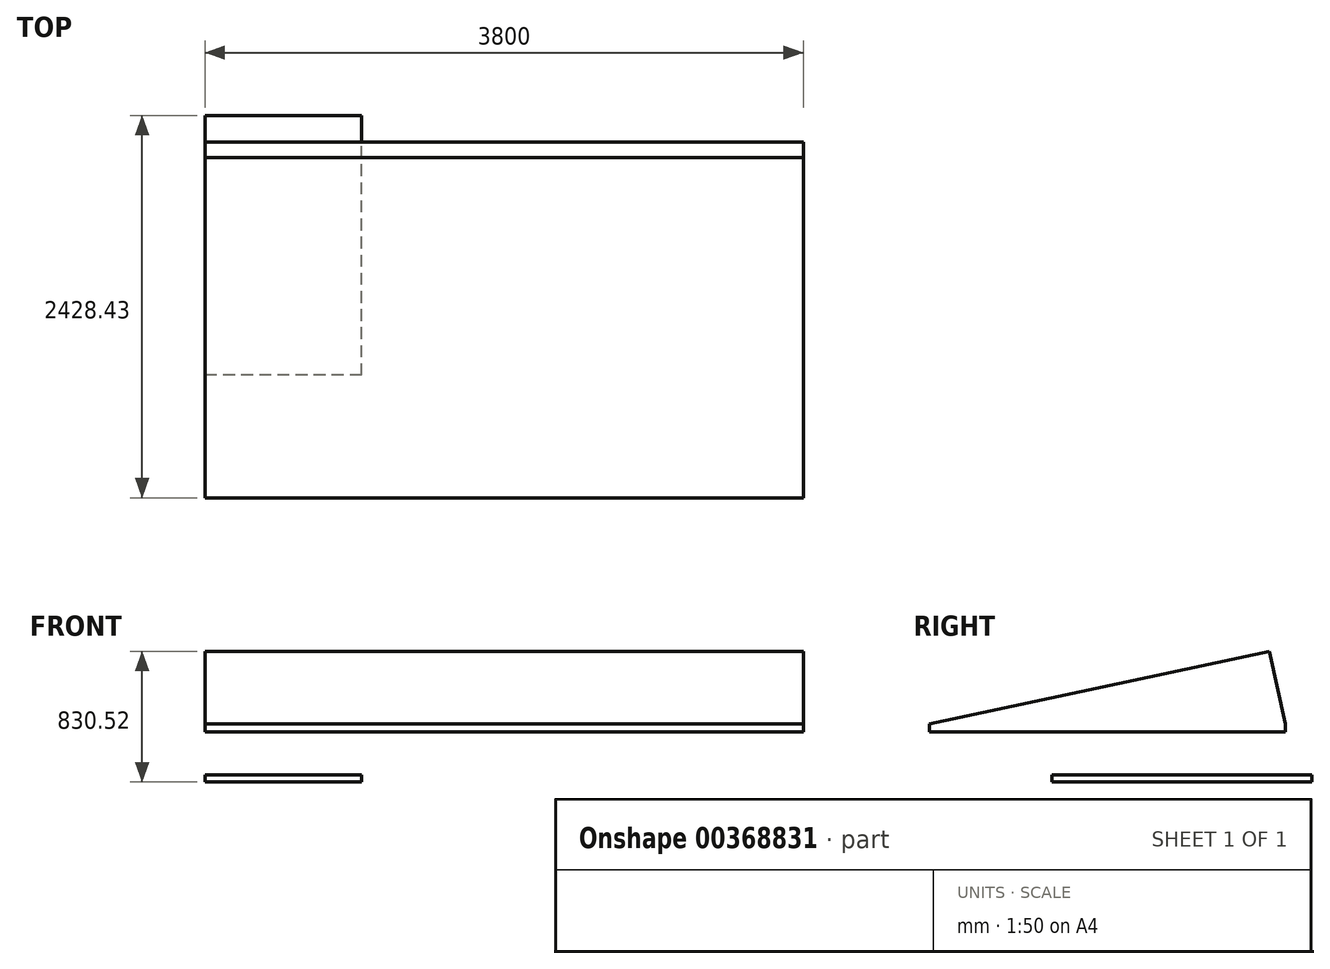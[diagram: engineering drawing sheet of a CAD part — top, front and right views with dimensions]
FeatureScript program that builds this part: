
annotation { "Feature Type Name" : "Feature", "Feature Type Description" : "" }
export const myFeature = defineFeature(function(context is Context, id is Id, definition is map)
    precondition{}
    {
        {
            var Q0;
            Q0=qCreatedBy(makeId("Right.planeOp"),FACE);
            var sketch = newSketch(context, id + "F0", { "sketchPlane" : qUnion([Q0])});
            skLineSegment(sketch, "E0.bottom", {"start": v(-70.47, 42.8) * mm, "end": v(1579.53, 42.8) * mm});
            skLineSegment(sketch, "E0.top", {"start": v(-70.47, -2.2) * mm, "end": v(1579.53, -2.2) * mm});
            skLineSegment(sketch, "E0.left", {"start": v(-70.47, 42.8) * mm, "end": v(-70.47, -2.2) * mm});
            skLineSegment(sketch, "E0.right", {"start": v(1579.53, 42.8) * mm, "end": v(1579.53, -2.2) * mm});
            skSolve(sketch);
        }
        {
            var Q0;
            Q0=makeQuery(id+"F0.imprint","IMPRINT",FACE,{"disambiguationData":[TD([[makeQuery(id+"F0.imprint","IMPRINT",EDGE,{"derivedFrom":sQuery(id+"F0.wireOp",EDGE,"E0.bottom")}),-1.0]])]});
            extrude(context, id + "F1", {"entities" : qUnion([Q0]), "depth" : 995 * mm});
        }
        {
            var Q0;
            Q0=qCreatedBy(makeId("Right.planeOp"),FACE);
            var sketch = newSketch(context, id + "F2", { "sketchPlane" : qUnion([Q0])});
            skLineSegment(sketch, "E1.bottom", {"start": v(-848.9, 366) * mm, "end": v(1411.1, 366) * mm});
            skLineSegment(sketch, "E1.top", {"start": v(-848.9, 316) * mm, "end": v(1411.1, 316) * mm});
            skLineSegment(sketch, "E1.left", {"start": v(-848.9, 366) * mm, "end": v(-848.9, 316) * mm});
            skLineSegment(sketch, "E1.right", {"start": v(1411.1, 366) * mm, "end": v(1411.1, 316) * mm});
            skSolve(sketch);
        }
        {
            var Q0;
            Q0 = qSketchRegion(id + "F2", true);
            extrude(context, id + "F3", {"entities" : qUnion([Q0]), "depth" : 3800 * mm});
        }
        {
            var Q0;
            Q0=makeQuery(id+"F3.opExtrude","CAP_FACE",FACE,{"disambiguationData":[OSD([sQuery(id+"F2.wireOp",EDGE,"E1.bottom"),sQuery(id+"F2.wireOp",EDGE,"E1.top"),sQuery(id+"F2.wireOp",EDGE,"E1.left"),sQuery(id+"F2.wireOp",EDGE,"E1.right")])],"isStart":false});
            var sketch = newSketch(context, id + "F4", { "sketchPlane" : qUnion([Q0])});
            skLineSegment(sketch, "E2", {"start": v(-848.9, 366) * mm, "end": v(1312.2, 828.3) * mm});
            skLineSegment(sketch, "E3", {"start": v(1312.2, 828.3) * mm, "end": v(1411.1, 366) * mm});
            skSolve(sketch);
        }
        {
            var Q0;
            Q0=makeQuery(id+"F4.imprint","IMPRINT",FACE,{"disambiguationData":[TD([[makeQuery(id+"F4.imprint","IMPRINT",EDGE,{"derivedFrom":sQuery(id+"F4.wireOp",EDGE,"E2")}),-1.0]])]});
            extrude(context, id + "F5", {"entities" : qUnion([Q0]), "operationType" : NewBodyOperationType.ADD, "depth" : -3800 * mm});
        }
    });
